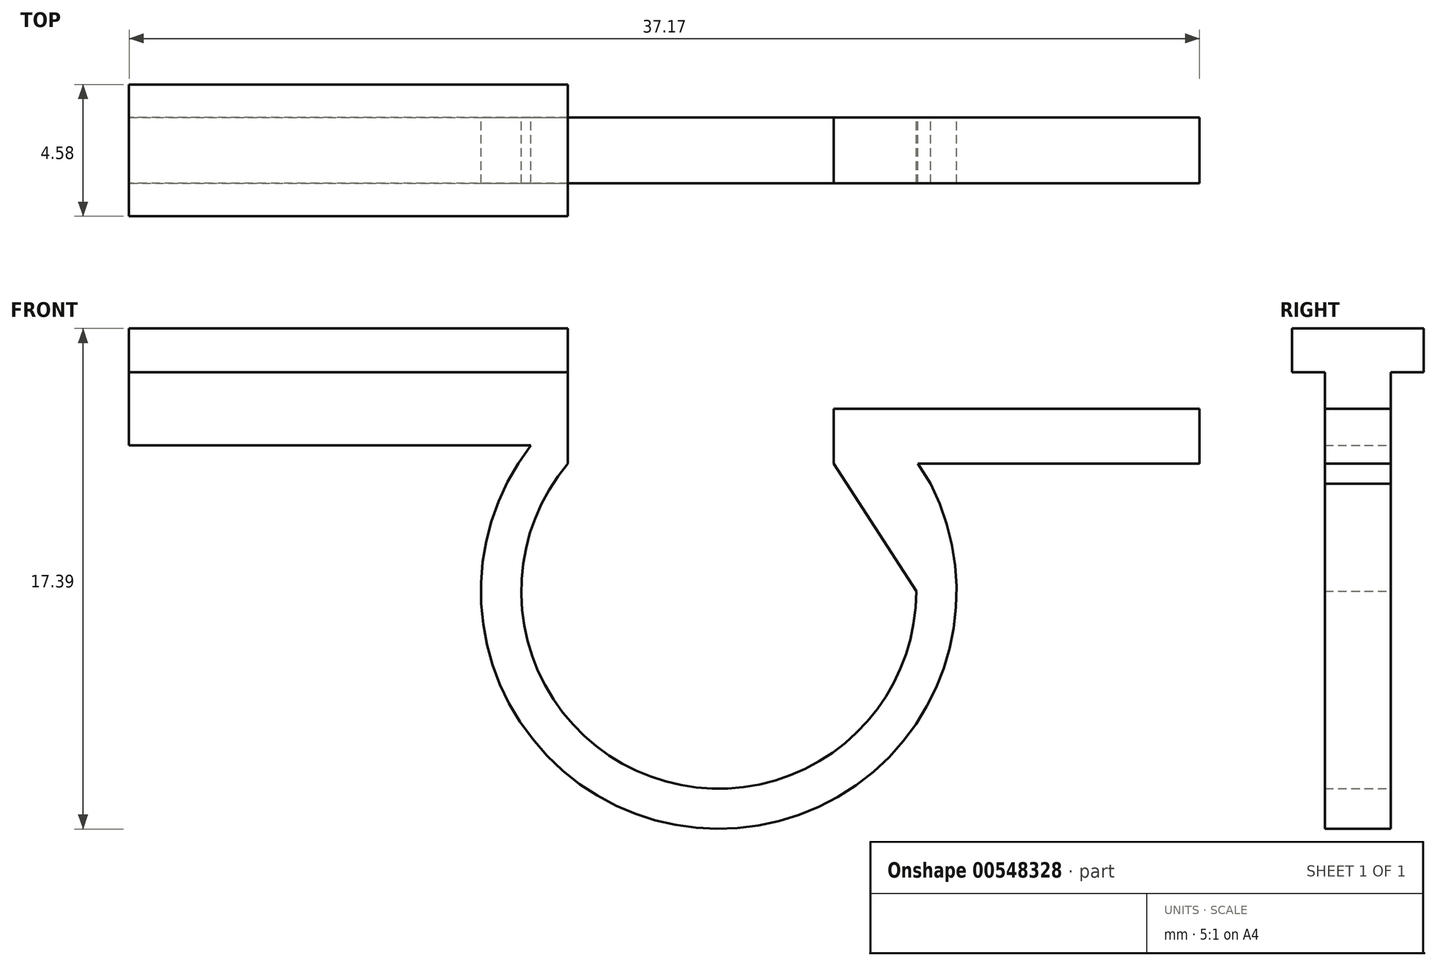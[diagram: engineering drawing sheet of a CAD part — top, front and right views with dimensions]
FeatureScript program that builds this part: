
annotation { "Feature Type Name" : "Feature", "Feature Type Description" : "" }
export const myFeature = defineFeature(function(context is Context, id is Id, definition is map)
    precondition{}
    {
        {
            var Q0;
            Q0=qCreatedBy(makeId("Front.planeOp"),FACE);
            var sketch = newSketch(context, id + "F0", { "sketchPlane" : qUnion([Q0])});
            skLineSegment(sketch, "E0", {"start": v(0, 0) * mm, "end": v(2.86, -4.43) * mm});
            skArc(sketch, "E1", {"start": v(2.86, -4.43) * mm, "mid": v(-6.36, -10.87) * mm, "end": v(-9.23, 0) * mm});
            skArc(sketch, "E2.0", {"start": v(3.37, -0.7) * mm, "mid": v(-4.79, -12.65) * mm, "end": v(-10.52, 0.63) * mm});
            skLineSegment(sketch, "E3", {"start": v(3.37, -0.7) * mm, "end": v(2.92, 0) * mm});
            skLineSegment(sketch, "E4", {"start": v(-10.52, 0.64) * mm, "end": v(-24.47, 0.64) * mm});
            skLineSegment(sketch, "E5", {"start": v(-24.47, 0.64) * mm, "end": v(-24.47, 3.18) * mm});
            skLineSegment(sketch, "E6", {"start": v(-24.47, 3.18) * mm, "end": v(-9.23, 3.18) * mm});
            skLineSegment(sketch, "E7", {"start": v(-9.23, 3.18) * mm, "end": v(-9.23, 0) * mm});
            skLineSegment(sketch, "E8", {"start": v(0, 0) * mm, "end": v(0, 1.9) * mm});
            skLineSegment(sketch, "E9", {"start": v(0, 1.9) * mm, "end": v(12.7, 1.9) * mm});
            skLineSegment(sketch, "E10", {"start": v(12.7, 1.9) * mm, "end": v(12.7, 0) * mm});
            skLineSegment(sketch, "E11", {"start": v(12.7, 0) * mm, "end": v(2.92, 0) * mm});
            skLineSegment(sketch, "E12", {"start": v(-10.52, 0.64) * mm, "end": v(-9.23, 0.64) * mm});
            skPoint(sketch, "E12.endSnap0", {"position": v(-9.23, 1.59) * mm});
            skSolve(sketch);
        }
        {
            var Q0;
            Q0=makeQuery(id+"F0.imprint","IMPRINT",FACE,{"disambiguationData":[TD([[makeQuery(id+"F0.imprint","IMPRINT",EDGE,{"derivedFrom":sQuery(id+"F0.wireOp",EDGE,"E0")}),1.0]])]});
            extrude(context, id + "F1", {"entities" : qUnion([Q0]), "endBound" : BoundingType.SYMMETRIC, "depth" : 2.3 * mm, "offsetDistance" : 25.4 * mm});
        }
        {
            var Q0;
            Q0=makeQuery(id+"F0.imprint","IMPRINT",FACE,{"disambiguationData":[TD([[makeQuery(id+"F0.imprint","IMPRINT",EDGE,{"derivedFrom":sQuery(id+"F0.wireOp",EDGE,"E4")}),-1.0]])]});
            var Q1;
            Q1 = qSketchRegion(id + "F3", true);
            extrude(context, id + "F2", {"entities" : qUnion([Q0, Q1]), "operationType" : NewBodyOperationType.ADD, "endBound" : BoundingType.SYMMETRIC, "depth" : 2.3 * mm, "offsetDistance" : 25.4 * mm});
        }
        {
            var Q0;
            Q0=makeQuery(id+"F2.opExtrude","SWEPT_FACE",FACE,{"disambiguationData":[OSD([sQuery(id+"F0.wireOp",EDGE,"E5")])]});
            var sketch = newSketch(context, id + "F3", { "sketchPlane" : qUnion([Q0])});
            skLineSegment(sketch, "E13", {"start": v(-2.29, 3.18) * mm, "end": v(-2.29, 4.7) * mm});
            skLineSegment(sketch, "E14", {"start": v(-2.29, 4.7) * mm, "end": v(0, 4.7) * mm});
            skLineSegment(sketch, "E15", {"start": v(-2.29, 3.18) * mm, "end": v(0, 3.18) * mm});
            skLineSegment(sketch, "E16.MirrorCS", {"start": v(2.29, 4.7) * mm, "end": v(0, 4.7) * mm});
            skLineSegment(sketch, "E17.MirrorCS", {"start": v(2.29, 3.18) * mm, "end": v(2.29, 4.7) * mm});
            skLineSegment(sketch, "E18.MirrorCS", {"start": v(2.29, 3.18) * mm, "end": v(0, 3.18) * mm});
            skSolve(sketch);
        }
        {
            var Q0;
            Q0 = qSketchRegion(id + "F3", true);
            var Q1;
            {var subQ0=sQuery(id+"F0.wireOp",EDGE,"E7");Q1=makeQuery(id+"F2.boolean.opBoolean","MERGE",FACE,{"derivedFrom":[makeQuery(id+"F1.opExtrude","SWEPT_FACE",FACE,{"disambiguationData":[OSD([subQ0])]}),makeQuery(id+"F2.opExtrude","SWEPT_FACE",FACE,{"disambiguationData":[OSD([subQ0])]})]});}
            extrude(context, id + "F4", {"entities" : qUnion([Q0]), "operationType" : NewBodyOperationType.ADD, "endBound" : BoundingType.UP_TO_SURFACE, "oppositeDirection" : true, "depth" : 25.4 * mm, "endBoundEntityFace" : qUnion([Q1]), "offsetDistance" : 25.4 * mm});
        }
    });
